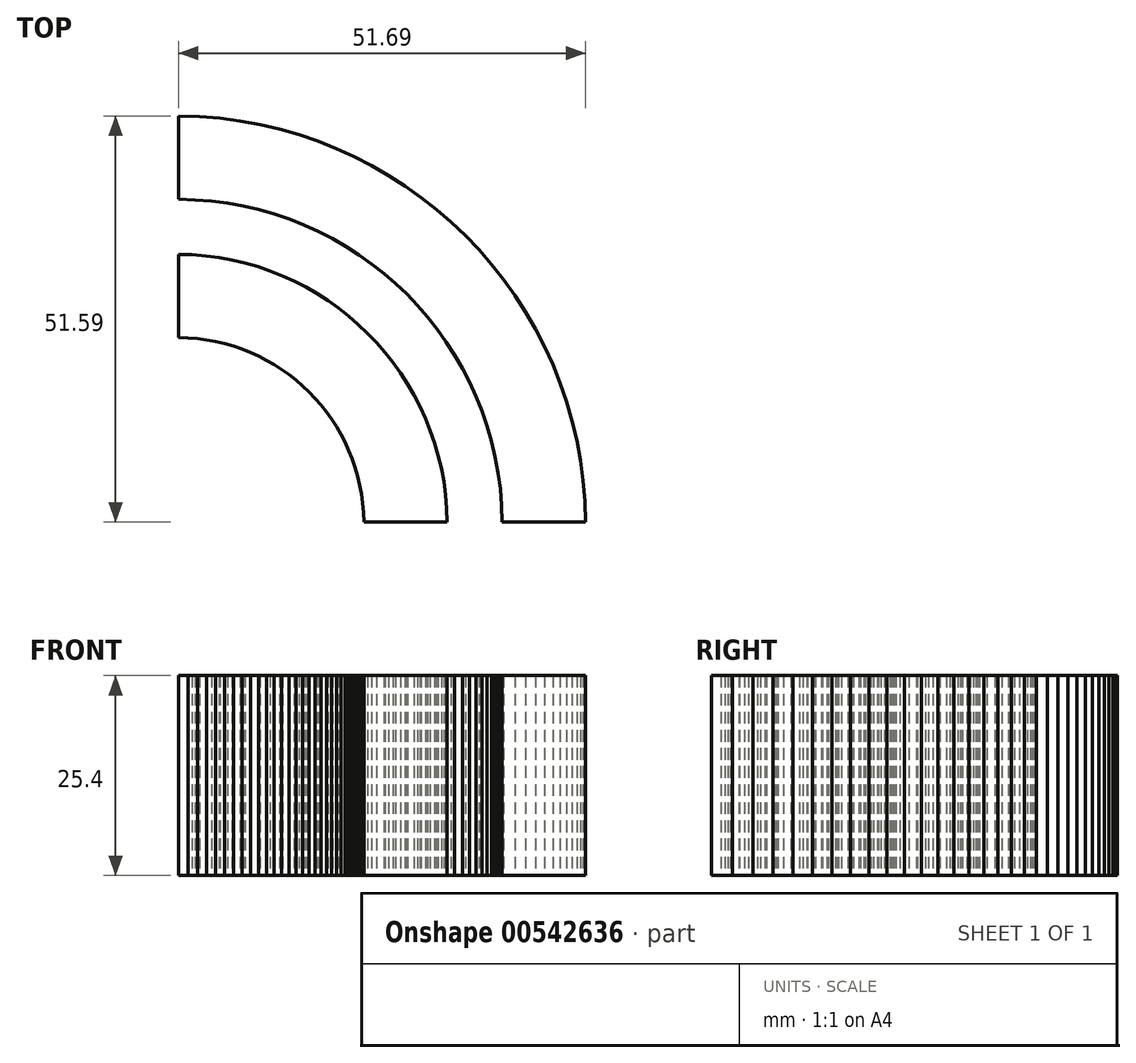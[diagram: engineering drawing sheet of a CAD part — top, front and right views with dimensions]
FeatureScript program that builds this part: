
annotation { "Feature Type Name" : "Feature", "Feature Type Description" : "" }
export const myFeature = defineFeature(function(context is Context, id is Id, definition is map)
    precondition{}
    {
        {
            var Q0;
            Q0=qCreatedBy(makeId("Top.planeOp"),FACE);
            var sketch = newSketch(context, id + "F0", { "sketchPlane" : qUnion([Q0])});
            skLineSegment(sketch, "E0", {"start": v(0.23, 64.99) * mm, "end": v(0.23, 64.66) * mm});
            skLineSegment(sketch, "E1", {"start": v(0.23, 64.66) * mm, "end": v(0.23, 64.33) * mm});
            skLineSegment(sketch, "E2", {"start": v(0.23, 64.33) * mm, "end": v(0.23, 64) * mm});
            skLineSegment(sketch, "E3", {"start": v(0.23, 64) * mm, "end": v(0.23, 63.66) * mm});
            skLineSegment(sketch, "E4", {"start": v(0.23, 63.66) * mm, "end": v(0.23, 63.33) * mm});
            skLineSegment(sketch, "E5", {"start": v(0.23, 63.33) * mm, "end": v(0.23, 63) * mm});
            skLineSegment(sketch, "E6", {"start": v(0.23, 63) * mm, "end": v(0.23, 62.67) * mm});
            skLineSegment(sketch, "E7", {"start": v(0.23, 62.67) * mm, "end": v(0.23, 62.34) * mm});
            skLineSegment(sketch, "E8", {"start": v(0.23, 62.34) * mm, "end": v(0.23, 62.01) * mm});
            skLineSegment(sketch, "E9", {"start": v(0.23, 62.01) * mm, "end": v(0.23, 61.68) * mm});
            skLineSegment(sketch, "E10", {"start": v(0.23, 61.68) * mm, "end": v(0.23, 61.35) * mm});
            skLineSegment(sketch, "E11", {"start": v(0.23, 61.35) * mm, "end": v(0.23, 61.02) * mm});
            skLineSegment(sketch, "E12", {"start": v(0.23, 61.02) * mm, "end": v(0.23, 60.69) * mm});
            skLineSegment(sketch, "E13", {"start": v(0.23, 60.69) * mm, "end": v(0.23, 60.36) * mm});
            skLineSegment(sketch, "E14", {"start": v(0.23, 60.36) * mm, "end": v(0.23, 60.03) * mm});
            skLineSegment(sketch, "E15", {"start": v(0.23, 60.03) * mm, "end": v(0.23, 59.7) * mm});
            skLineSegment(sketch, "E16", {"start": v(0.23, 59.7) * mm, "end": v(0.23, 59.36) * mm});
            skLineSegment(sketch, "E17", {"start": v(0.23, 59.36) * mm, "end": v(0.23, 59.03) * mm});
            skLineSegment(sketch, "E18", {"start": v(0.23, 59.03) * mm, "end": v(0.23, 58.7) * mm});
            skLineSegment(sketch, "E19", {"start": v(0.23, 58.7) * mm, "end": v(0.23, 58.37) * mm});
            skLineSegment(sketch, "E20", {"start": v(0.23, 58.37) * mm, "end": v(0.23, 58.04) * mm});
            skLineSegment(sketch, "E21", {"start": v(0.23, 58.04) * mm, "end": v(0.23, 57.7) * mm});
            skLineSegment(sketch, "E22", {"start": v(0.23, 57.7) * mm, "end": v(0.23, 57.38) * mm});
            skLineSegment(sketch, "E23", {"start": v(0.23, 57.38) * mm, "end": v(0.23, 57.05) * mm});
            skLineSegment(sketch, "E24", {"start": v(0.23, 57.05) * mm, "end": v(0.23, 56.72) * mm});
            skLineSegment(sketch, "E25", {"start": v(0.23, 56.72) * mm, "end": v(0.23, 56.39) * mm});
            skLineSegment(sketch, "E26", {"start": v(0.23, 56.39) * mm, "end": v(0.23, 56.06) * mm});
            skLineSegment(sketch, "E27", {"start": v(0.23, 56.06) * mm, "end": v(0.23, 55.72) * mm});
            skLineSegment(sketch, "E28", {"start": v(0.23, 55.72) * mm, "end": v(0.23, 55.4) * mm});
            skLineSegment(sketch, "E29", {"start": v(0.23, 55.4) * mm, "end": v(0.23, 55.06) * mm});
            skLineSegment(sketch, "E30", {"start": v(0.23, 55.06) * mm, "end": v(0.23, 54.73) * mm});
            skLineSegment(sketch, "E31", {"start": v(0.23, 54.73) * mm, "end": v(0.23, 54.4) * mm});
            skLineSegment(sketch, "E32", {"start": v(0.23, 54.4) * mm, "end": v(1.43, 54.36) * mm});
            skLineSegment(sketch, "E33", {"start": v(1.43, 54.36) * mm, "end": v(2.63, 54.26) * mm});
            skLineSegment(sketch, "E34", {"start": v(2.63, 54.26) * mm, "end": v(3.8, 54.1) * mm});
            skLineSegment(sketch, "E35", {"start": v(3.8, 54.1) * mm, "end": v(4.95, 53.9) * mm});
            skLineSegment(sketch, "E36", {"start": v(4.95, 53.9) * mm, "end": v(6.09, 53.62) * mm});
            skLineSegment(sketch, "E37", {"start": v(6.09, 53.62) * mm, "end": v(7.2, 53.3) * mm});
            skLineSegment(sketch, "E38", {"start": v(7.2, 53.3) * mm, "end": v(8.29, 52.93) * mm});
            skLineSegment(sketch, "E39", {"start": v(8.29, 52.93) * mm, "end": v(9.35, 52.51) * mm});
            skLineSegment(sketch, "E40", {"start": v(9.35, 52.51) * mm, "end": v(10.39, 52.04) * mm});
            skLineSegment(sketch, "E41", {"start": v(10.39, 52.04) * mm, "end": v(11.4, 51.52) * mm});
            skLineSegment(sketch, "E42", {"start": v(11.4, 51.52) * mm, "end": v(12.38, 50.96) * mm});
            skLineSegment(sketch, "E43", {"start": v(12.38, 50.96) * mm, "end": v(13.33, 50.35) * mm});
            skLineSegment(sketch, "E44", {"start": v(13.33, 50.35) * mm, "end": v(14.24, 49.7) * mm});
            skLineSegment(sketch, "E45", {"start": v(14.24, 49.7) * mm, "end": v(15.13, 49) * mm});
            skLineSegment(sketch, "E46", {"start": v(15.13, 49) * mm, "end": v(15.98, 48.27) * mm});
            skLineSegment(sketch, "E47", {"start": v(15.98, 48.27) * mm, "end": v(16.8, 47.5) * mm});
            skLineSegment(sketch, "E48", {"start": v(16.8, 47.5) * mm, "end": v(17.57, 46.7) * mm});
            skLineSegment(sketch, "E49", {"start": v(17.57, 46.7) * mm, "end": v(18.3, 45.84) * mm});
            skLineSegment(sketch, "E50", {"start": v(18.3, 45.84) * mm, "end": v(19, 44.96) * mm});
            skLineSegment(sketch, "E51", {"start": v(19, 44.96) * mm, "end": v(19.66, 44.05) * mm});
            skLineSegment(sketch, "E52", {"start": v(19.66, 44.05) * mm, "end": v(20.27, 43.1) * mm});
            skLineSegment(sketch, "E53", {"start": v(20.27, 43.1) * mm, "end": v(20.84, 42.12) * mm});
            skLineSegment(sketch, "E54", {"start": v(20.84, 42.12) * mm, "end": v(21.36, 41.12) * mm});
            skLineSegment(sketch, "E55", {"start": v(21.36, 41.12) * mm, "end": v(21.84, 40.08) * mm});
            skLineSegment(sketch, "E56", {"start": v(21.84, 40.08) * mm, "end": v(22.26, 39.02) * mm});
            skLineSegment(sketch, "E57", {"start": v(22.26, 39.02) * mm, "end": v(22.64, 37.94) * mm});
            skLineSegment(sketch, "E58", {"start": v(22.64, 37.94) * mm, "end": v(22.96, 36.83) * mm});
            skLineSegment(sketch, "E59", {"start": v(22.96, 36.83) * mm, "end": v(23.23, 35.7) * mm});
            skLineSegment(sketch, "E60", {"start": v(23.23, 35.7) * mm, "end": v(23.45, 34.54) * mm});
            skLineSegment(sketch, "E61", {"start": v(23.45, 34.54) * mm, "end": v(23.61, 33.37) * mm});
            skLineSegment(sketch, "E62", {"start": v(23.61, 33.37) * mm, "end": v(23.72, 32.18) * mm});
            skLineSegment(sketch, "E63", {"start": v(23.72, 32.18) * mm, "end": v(23.77, 30.97) * mm});
            skLineSegment(sketch, "E64", {"start": v(23.77, 30.97) * mm, "end": v(24.1, 30.97) * mm});
            skLineSegment(sketch, "E65", {"start": v(24.1, 30.97) * mm, "end": v(24.43, 30.97) * mm});
            skLineSegment(sketch, "E66", {"start": v(24.43, 30.97) * mm, "end": v(24.76, 30.97) * mm});
            skLineSegment(sketch, "E67", {"start": v(24.76, 30.97) * mm, "end": v(25.09, 30.97) * mm});
            skLineSegment(sketch, "E68", {"start": v(25.09, 30.97) * mm, "end": v(25.42, 30.97) * mm});
            skLineSegment(sketch, "E69", {"start": v(25.42, 30.97) * mm, "end": v(25.75, 30.97) * mm});
            skLineSegment(sketch, "E70", {"start": v(25.75, 30.97) * mm, "end": v(26.08, 30.97) * mm});
            skLineSegment(sketch, "E71", {"start": v(26.08, 30.97) * mm, "end": v(26.41, 30.97) * mm});
            skLineSegment(sketch, "E72", {"start": v(26.41, 30.97) * mm, "end": v(26.74, 30.97) * mm});
            skLineSegment(sketch, "E73", {"start": v(26.74, 30.97) * mm, "end": v(27.07, 30.97) * mm});
            skLineSegment(sketch, "E74", {"start": v(27.07, 30.97) * mm, "end": v(27.4, 30.97) * mm});
            skLineSegment(sketch, "E75", {"start": v(27.4, 30.97) * mm, "end": v(27.74, 30.97) * mm});
            skLineSegment(sketch, "E76", {"start": v(27.74, 30.97) * mm, "end": v(28.07, 30.97) * mm});
            skLineSegment(sketch, "E77", {"start": v(28.07, 30.97) * mm, "end": v(28.4, 30.97) * mm});
            skLineSegment(sketch, "E78", {"start": v(28.4, 30.97) * mm, "end": v(28.73, 30.97) * mm});
            skLineSegment(sketch, "E79", {"start": v(28.73, 30.97) * mm, "end": v(29.06, 30.97) * mm});
            skLineSegment(sketch, "E80", {"start": v(29.06, 30.97) * mm, "end": v(29.4, 30.97) * mm});
            skLineSegment(sketch, "E81", {"start": v(29.4, 30.97) * mm, "end": v(29.72, 30.97) * mm});
            skLineSegment(sketch, "E82", {"start": v(29.72, 30.97) * mm, "end": v(30.05, 30.97) * mm});
            skLineSegment(sketch, "E83", {"start": v(30.05, 30.97) * mm, "end": v(30.38, 30.97) * mm});
            skLineSegment(sketch, "E84", {"start": v(30.38, 30.97) * mm, "end": v(30.71, 30.97) * mm});
            skLineSegment(sketch, "E85", {"start": v(30.71, 30.97) * mm, "end": v(31.05, 30.97) * mm});
            skLineSegment(sketch, "E86", {"start": v(31.05, 30.97) * mm, "end": v(31.38, 30.97) * mm});
            skLineSegment(sketch, "E87", {"start": v(31.38, 30.97) * mm, "end": v(31.7, 30.97) * mm});
            skLineSegment(sketch, "E88", {"start": v(31.7, 30.97) * mm, "end": v(32.04, 30.97) * mm});
            skLineSegment(sketch, "E89", {"start": v(32.04, 30.97) * mm, "end": v(32.37, 30.97) * mm});
            skLineSegment(sketch, "E90", {"start": v(32.37, 30.97) * mm, "end": v(32.7, 30.97) * mm});
            skLineSegment(sketch, "E91", {"start": v(32.7, 30.97) * mm, "end": v(33.03, 30.97) * mm});
            skLineSegment(sketch, "E92", {"start": v(33.03, 30.97) * mm, "end": v(33.36, 30.97) * mm});
            skLineSegment(sketch, "E93", {"start": v(33.36, 30.97) * mm, "end": v(33.7, 30.97) * mm});
            skLineSegment(sketch, "E94", {"start": v(33.7, 30.97) * mm, "end": v(34.02, 30.97) * mm});
            skLineSegment(sketch, "E95", {"start": v(34.02, 30.97) * mm, "end": v(34.35, 30.97) * mm});
            skLineSegment(sketch, "E96", {"start": v(34.35, 30.97) * mm, "end": v(34.3, 32.71) * mm});
            skLineSegment(sketch, "E97", {"start": v(34.3, 32.71) * mm, "end": v(34.15, 34.43) * mm});
            skLineSegment(sketch, "E98", {"start": v(34.15, 34.43) * mm, "end": v(33.91, 36.13) * mm});
            skLineSegment(sketch, "E99", {"start": v(33.91, 36.13) * mm, "end": v(33.6, 37.8) * mm});
            skLineSegment(sketch, "E100", {"start": v(33.6, 37.8) * mm, "end": v(33.2, 39.43) * mm});
            skLineSegment(sketch, "E101", {"start": v(33.2, 39.43) * mm, "end": v(32.74, 41.04) * mm});
            skLineSegment(sketch, "E102", {"start": v(32.74, 41.04) * mm, "end": v(32.2, 42.61) * mm});
            skLineSegment(sketch, "E103", {"start": v(32.2, 42.61) * mm, "end": v(31.57, 44.15) * mm});
            skLineSegment(sketch, "E104", {"start": v(31.57, 44.15) * mm, "end": v(30.88, 45.65) * mm});
            skLineSegment(sketch, "E105", {"start": v(30.88, 45.65) * mm, "end": v(30.12, 47.12) * mm});
            skLineSegment(sketch, "E106", {"start": v(30.12, 47.12) * mm, "end": v(29.3, 48.54) * mm});
            skLineSegment(sketch, "E107", {"start": v(29.3, 48.54) * mm, "end": v(28.4, 49.91) * mm});
            skLineSegment(sketch, "E108", {"start": v(28.4, 49.91) * mm, "end": v(27.45, 51.24) * mm});
            skLineSegment(sketch, "E109", {"start": v(27.45, 51.24) * mm, "end": v(26.43, 52.53) * mm});
            skLineSegment(sketch, "E110", {"start": v(26.43, 52.53) * mm, "end": v(25.36, 53.76) * mm});
            skLineSegment(sketch, "E111", {"start": v(25.36, 53.76) * mm, "end": v(24.23, 54.94) * mm});
            skLineSegment(sketch, "E112", {"start": v(24.23, 54.94) * mm, "end": v(23.05, 56.07) * mm});
            skLineSegment(sketch, "E113", {"start": v(23.05, 56.07) * mm, "end": v(21.81, 57.14) * mm});
            skLineSegment(sketch, "E114", {"start": v(21.81, 57.14) * mm, "end": v(20.53, 58.15) * mm});
            skLineSegment(sketch, "E115", {"start": v(20.53, 58.15) * mm, "end": v(19.2, 59.1) * mm});
            skLineSegment(sketch, "E116", {"start": v(19.2, 59.1) * mm, "end": v(17.81, 59.98) * mm});
            skLineSegment(sketch, "E117", {"start": v(17.81, 59.98) * mm, "end": v(16.39, 60.8) * mm});
            skLineSegment(sketch, "E118", {"start": v(16.39, 60.8) * mm, "end": v(14.92, 61.56) * mm});
            skLineSegment(sketch, "E119", {"start": v(14.92, 61.56) * mm, "end": v(13.42, 62.25) * mm});
            skLineSegment(sketch, "E120", {"start": v(13.42, 62.25) * mm, "end": v(11.88, 62.86) * mm});
            skLineSegment(sketch, "E121", {"start": v(11.88, 62.86) * mm, "end": v(10.3, 63.4) * mm});
            skLineSegment(sketch, "E122", {"start": v(10.3, 63.4) * mm, "end": v(8.7, 63.87) * mm});
            skLineSegment(sketch, "E123", {"start": v(8.7, 63.87) * mm, "end": v(7.05, 64.26) * mm});
            skLineSegment(sketch, "E124", {"start": v(7.05, 64.26) * mm, "end": v(5.38, 64.56) * mm});
            skLineSegment(sketch, "E125", {"start": v(5.38, 64.56) * mm, "end": v(3.69, 64.8) * mm});
            skLineSegment(sketch, "E126", {"start": v(3.69, 64.8) * mm, "end": v(1.97, 64.93) * mm});
            skLineSegment(sketch, "E127", {"start": v(1.97, 64.93) * mm, "end": v(0.23, 64.99) * mm});
            skLineSegment(sketch, "E128", {"start": v(0.23, 82.56) * mm, "end": v(0.23, 82.23) * mm});
            skLineSegment(sketch, "E129", {"start": v(0.23, 82.23) * mm, "end": v(0.23, 81.9) * mm});
            skLineSegment(sketch, "E130", {"start": v(0.23, 81.9) * mm, "end": v(0.23, 81.56) * mm});
            skLineSegment(sketch, "E131", {"start": v(0.23, 81.56) * mm, "end": v(0.23, 81.23) * mm});
            skLineSegment(sketch, "E132", {"start": v(0.23, 81.23) * mm, "end": v(0.23, 80.9) * mm});
            skLineSegment(sketch, "E133", {"start": v(0.23, 80.9) * mm, "end": v(0.23, 80.57) * mm});
            skLineSegment(sketch, "E134", {"start": v(0.23, 80.57) * mm, "end": v(0.23, 80.24) * mm});
            skLineSegment(sketch, "E135", {"start": v(0.23, 80.24) * mm, "end": v(0.23, 79.91) * mm});
            skLineSegment(sketch, "E136", {"start": v(0.23, 79.91) * mm, "end": v(0.23, 79.58) * mm});
            skLineSegment(sketch, "E137", {"start": v(0.23, 79.58) * mm, "end": v(0.23, 79.25) * mm});
            skLineSegment(sketch, "E138", {"start": v(0.23, 79.25) * mm, "end": v(0.23, 78.92) * mm});
            skLineSegment(sketch, "E139", {"start": v(0.23, 78.92) * mm, "end": v(0.23, 78.59) * mm});
            skLineSegment(sketch, "E140", {"start": v(0.23, 78.59) * mm, "end": v(0.23, 78.26) * mm});
            skLineSegment(sketch, "E141", {"start": v(0.23, 78.26) * mm, "end": v(0.23, 77.93) * mm});
            skLineSegment(sketch, "E142", {"start": v(0.23, 77.93) * mm, "end": v(0.23, 77.6) * mm});
            skLineSegment(sketch, "E143", {"start": v(0.23, 77.6) * mm, "end": v(0.23, 77.26) * mm});
            skLineSegment(sketch, "E144", {"start": v(0.23, 77.26) * mm, "end": v(0.23, 76.93) * mm});
            skLineSegment(sketch, "E145", {"start": v(0.23, 76.93) * mm, "end": v(0.23, 76.6) * mm});
            skLineSegment(sketch, "E146", {"start": v(0.23, 76.6) * mm, "end": v(0.23, 76.27) * mm});
            skLineSegment(sketch, "E147", {"start": v(0.23, 76.27) * mm, "end": v(0.23, 75.94) * mm});
            skLineSegment(sketch, "E148", {"start": v(0.23, 75.94) * mm, "end": v(0.23, 75.61) * mm});
            skLineSegment(sketch, "E149", {"start": v(0.23, 75.61) * mm, "end": v(0.23, 75.28) * mm});
            skLineSegment(sketch, "E150", {"start": v(0.23, 75.28) * mm, "end": v(0.23, 74.95) * mm});
            skLineSegment(sketch, "E151", {"start": v(0.23, 74.95) * mm, "end": v(0.23, 74.62) * mm});
            skLineSegment(sketch, "E152", {"start": v(0.23, 74.62) * mm, "end": v(0.23, 74.29) * mm});
            skLineSegment(sketch, "E153", {"start": v(0.23, 74.29) * mm, "end": v(0.23, 73.96) * mm});
            skLineSegment(sketch, "E154", {"start": v(0.23, 73.96) * mm, "end": v(0.23, 73.63) * mm});
            skLineSegment(sketch, "E155", {"start": v(0.23, 73.63) * mm, "end": v(0.23, 73.3) * mm});
            skLineSegment(sketch, "E156", {"start": v(0.23, 73.3) * mm, "end": v(0.23, 72.96) * mm});
            skLineSegment(sketch, "E157", {"start": v(0.23, 72.96) * mm, "end": v(0.23, 72.63) * mm});
            skLineSegment(sketch, "E158", {"start": v(0.23, 72.63) * mm, "end": v(0.23, 72.3) * mm});
            skLineSegment(sketch, "E159", {"start": v(0.23, 72.3) * mm, "end": v(0.23, 71.97) * mm});
            skLineSegment(sketch, "E160", {"start": v(0.23, 71.97) * mm, "end": v(2.34, 71.9) * mm});
            skLineSegment(sketch, "E161", {"start": v(2.34, 71.9) * mm, "end": v(4.42, 71.74) * mm});
            skLineSegment(sketch, "E162", {"start": v(4.42, 71.74) * mm, "end": v(6.48, 71.47) * mm});
            skLineSegment(sketch, "E163", {"start": v(6.48, 71.47) * mm, "end": v(8.5, 71.1) * mm});
            skLineSegment(sketch, "E164", {"start": v(8.5, 71.1) * mm, "end": v(10.48, 70.64) * mm});
            skLineSegment(sketch, "E165", {"start": v(10.48, 70.64) * mm, "end": v(12.43, 70.09) * mm});
            skLineSegment(sketch, "E166", {"start": v(12.43, 70.09) * mm, "end": v(14.33, 69.44) * mm});
            skLineSegment(sketch, "E167", {"start": v(14.33, 69.44) * mm, "end": v(16.2, 68.7) * mm});
            skLineSegment(sketch, "E168", {"start": v(16.2, 68.7) * mm, "end": v(18, 67.88) * mm});
            skLineSegment(sketch, "E169", {"start": v(18, 67.88) * mm, "end": v(19.77, 66.97) * mm});
            skLineSegment(sketch, "E170", {"start": v(19.77, 66.97) * mm, "end": v(21.49, 65.99) * mm});
            skLineSegment(sketch, "E171", {"start": v(21.49, 65.99) * mm, "end": v(23.15, 64.92) * mm});
            skLineSegment(sketch, "E172", {"start": v(23.15, 64.92) * mm, "end": v(24.76, 63.78) * mm});
            skLineSegment(sketch, "E173", {"start": v(24.76, 63.78) * mm, "end": v(26.3, 62.57) * mm});
            skLineSegment(sketch, "E174", {"start": v(26.3, 62.57) * mm, "end": v(27.8, 61.28) * mm});
            skLineSegment(sketch, "E175", {"start": v(27.8, 61.28) * mm, "end": v(29.22, 59.93) * mm});
            skLineSegment(sketch, "E176", {"start": v(29.22, 59.93) * mm, "end": v(30.58, 58.5) * mm});
            skLineSegment(sketch, "E177", {"start": v(30.58, 58.5) * mm, "end": v(31.87, 57.02) * mm});
            skLineSegment(sketch, "E178", {"start": v(31.87, 57.02) * mm, "end": v(33.08, 55.48) * mm});
            skLineSegment(sketch, "E179", {"start": v(33.08, 55.48) * mm, "end": v(34.23, 53.87) * mm});
            skLineSegment(sketch, "E180", {"start": v(34.23, 53.87) * mm, "end": v(35.3, 52.21) * mm});
            skLineSegment(sketch, "E181", {"start": v(35.3, 52.21) * mm, "end": v(36.3, 50.5) * mm});
            skLineSegment(sketch, "E182", {"start": v(36.3, 50.5) * mm, "end": v(37.2, 48.74) * mm});
            skLineSegment(sketch, "E183", {"start": v(37.2, 48.74) * mm, "end": v(38.03, 46.92) * mm});
            skLineSegment(sketch, "E184", {"start": v(38.03, 46.92) * mm, "end": v(38.77, 45.06) * mm});
            skLineSegment(sketch, "E185", {"start": v(38.77, 45.06) * mm, "end": v(39.42, 43.16) * mm});
            skLineSegment(sketch, "E186", {"start": v(39.42, 43.16) * mm, "end": v(39.98, 41.22) * mm});
            skLineSegment(sketch, "E187", {"start": v(39.98, 41.22) * mm, "end": v(40.45, 39.24) * mm});
            skLineSegment(sketch, "E188", {"start": v(40.45, 39.24) * mm, "end": v(40.82, 37.22) * mm});
            skLineSegment(sketch, "E189", {"start": v(40.82, 37.22) * mm, "end": v(41.1, 35.17) * mm});
            skLineSegment(sketch, "E190", {"start": v(41.1, 35.17) * mm, "end": v(41.27, 33.08) * mm});
            skLineSegment(sketch, "E191", {"start": v(41.27, 33.08) * mm, "end": v(41.34, 30.97) * mm});
            skLineSegment(sketch, "E192", {"start": v(41.34, 30.97) * mm, "end": v(41.67, 30.97) * mm});
            skLineSegment(sketch, "E193", {"start": v(41.67, 30.97) * mm, "end": v(42, 30.97) * mm});
            skLineSegment(sketch, "E194", {"start": v(42, 30.97) * mm, "end": v(42.33, 30.97) * mm});
            skLineSegment(sketch, "E195", {"start": v(42.33, 30.97) * mm, "end": v(42.66, 30.97) * mm});
            skLineSegment(sketch, "E196", {"start": v(42.66, 30.97) * mm, "end": v(43, 30.97) * mm});
            skLineSegment(sketch, "E197", {"start": v(43, 30.97) * mm, "end": v(43.32, 30.97) * mm});
            skLineSegment(sketch, "E198", {"start": v(43.32, 30.97) * mm, "end": v(43.65, 30.97) * mm});
            skLineSegment(sketch, "E199", {"start": v(43.65, 30.97) * mm, "end": v(43.99, 30.97) * mm});
            skLineSegment(sketch, "E200", {"start": v(43.99, 30.97) * mm, "end": v(44.32, 30.97) * mm});
            skLineSegment(sketch, "E201", {"start": v(44.32, 30.97) * mm, "end": v(44.65, 30.97) * mm});
            skLineSegment(sketch, "E202", {"start": v(44.65, 30.97) * mm, "end": v(44.98, 30.97) * mm});
            skLineSegment(sketch, "E203", {"start": v(44.98, 30.97) * mm, "end": v(45.3, 30.97) * mm});
            skLineSegment(sketch, "E204", {"start": v(45.3, 30.97) * mm, "end": v(45.64, 30.97) * mm});
            skLineSegment(sketch, "E205", {"start": v(45.64, 30.97) * mm, "end": v(45.97, 30.97) * mm});
            skLineSegment(sketch, "E206", {"start": v(45.97, 30.97) * mm, "end": v(46.3, 30.97) * mm});
            skLineSegment(sketch, "E207", {"start": v(46.3, 30.97) * mm, "end": v(46.63, 30.97) * mm});
            skLineSegment(sketch, "E208", {"start": v(46.63, 30.97) * mm, "end": v(46.96, 30.97) * mm});
            skLineSegment(sketch, "E209", {"start": v(46.96, 30.97) * mm, "end": v(47.3, 30.97) * mm});
            skLineSegment(sketch, "E210", {"start": v(47.3, 30.97) * mm, "end": v(47.62, 30.97) * mm});
            skLineSegment(sketch, "E211", {"start": v(47.62, 30.97) * mm, "end": v(47.95, 30.97) * mm});
            skLineSegment(sketch, "E212", {"start": v(47.95, 30.97) * mm, "end": v(48.28, 30.97) * mm});
            skLineSegment(sketch, "E213", {"start": v(48.28, 30.97) * mm, "end": v(48.62, 30.97) * mm});
            skLineSegment(sketch, "E214", {"start": v(48.62, 30.97) * mm, "end": v(48.95, 30.97) * mm});
            skLineSegment(sketch, "E215", {"start": v(48.95, 30.97) * mm, "end": v(49.28, 30.97) * mm});
            skLineSegment(sketch, "E216", {"start": v(49.28, 30.97) * mm, "end": v(49.6, 30.97) * mm});
            skLineSegment(sketch, "E217", {"start": v(49.6, 30.97) * mm, "end": v(49.94, 30.97) * mm});
            skLineSegment(sketch, "E218", {"start": v(49.94, 30.97) * mm, "end": v(50.27, 30.97) * mm});
            skLineSegment(sketch, "E219", {"start": v(50.27, 30.97) * mm, "end": v(50.6, 30.97) * mm});
            skLineSegment(sketch, "E220", {"start": v(50.6, 30.97) * mm, "end": v(50.93, 30.97) * mm});
            skLineSegment(sketch, "E221", {"start": v(50.93, 30.97) * mm, "end": v(51.26, 30.97) * mm});
            skLineSegment(sketch, "E222", {"start": v(51.26, 30.97) * mm, "end": v(51.6, 30.97) * mm});
            skLineSegment(sketch, "E223", {"start": v(51.6, 30.97) * mm, "end": v(51.92, 30.97) * mm});
            skLineSegment(sketch, "E224", {"start": v(51.92, 30.97) * mm, "end": v(51.84, 33.62) * mm});
            skLineSegment(sketch, "E225", {"start": v(51.84, 33.62) * mm, "end": v(51.62, 36.23) * mm});
            skLineSegment(sketch, "E226", {"start": v(51.62, 36.23) * mm, "end": v(51.28, 38.8) * mm});
            skLineSegment(sketch, "E227", {"start": v(51.28, 38.8) * mm, "end": v(50.81, 41.33) * mm});
            skLineSegment(sketch, "E228", {"start": v(50.81, 41.33) * mm, "end": v(50.22, 43.82) * mm});
            skLineSegment(sketch, "E229", {"start": v(50.22, 43.82) * mm, "end": v(49.52, 46.26) * mm});
            skLineSegment(sketch, "E230", {"start": v(49.52, 46.26) * mm, "end": v(48.7, 48.65) * mm});
            skLineSegment(sketch, "E231", {"start": v(48.7, 48.65) * mm, "end": v(47.76, 50.99) * mm});
            skLineSegment(sketch, "E232", {"start": v(47.76, 50.99) * mm, "end": v(46.72, 53.27) * mm});
            skLineSegment(sketch, "E233", {"start": v(46.72, 53.27) * mm, "end": v(45.57, 55.49) * mm});
            skLineSegment(sketch, "E234", {"start": v(45.57, 55.49) * mm, "end": v(44.32, 57.65) * mm});
            skLineSegment(sketch, "E235", {"start": v(44.32, 57.65) * mm, "end": v(42.97, 59.73) * mm});
            skLineSegment(sketch, "E236", {"start": v(42.97, 59.73) * mm, "end": v(41.53, 61.75) * mm});
            skLineSegment(sketch, "E237", {"start": v(41.53, 61.75) * mm, "end": v(40, 63.7) * mm});
            skLineSegment(sketch, "E238", {"start": v(40, 63.7) * mm, "end": v(38.37, 65.57) * mm});
            skLineSegment(sketch, "E239", {"start": v(38.37, 65.57) * mm, "end": v(36.65, 67.36) * mm});
            skLineSegment(sketch, "E240", {"start": v(36.65, 67.36) * mm, "end": v(34.86, 69.07) * mm});
            skLineSegment(sketch, "E241", {"start": v(34.86, 69.07) * mm, "end": v(32.99, 70.7) * mm});
            skLineSegment(sketch, "E242", {"start": v(32.99, 70.7) * mm, "end": v(31.04, 72.22) * mm});
            skLineSegment(sketch, "E243", {"start": v(31.04, 72.22) * mm, "end": v(29.01, 73.66) * mm});
            skLineSegment(sketch, "E244", {"start": v(29.01, 73.66) * mm, "end": v(26.92, 75) * mm});
            skLineSegment(sketch, "E245", {"start": v(26.92, 75) * mm, "end": v(24.76, 76.25) * mm});
            skLineSegment(sketch, "E246", {"start": v(24.76, 76.25) * mm, "end": v(22.54, 77.4) * mm});
            skLineSegment(sketch, "E247", {"start": v(22.54, 77.4) * mm, "end": v(20.26, 78.44) * mm});
            skLineSegment(sketch, "E248", {"start": v(20.26, 78.44) * mm, "end": v(17.92, 79.36) * mm});
            skLineSegment(sketch, "E249", {"start": v(17.92, 79.36) * mm, "end": v(15.53, 80.18) * mm});
            skLineSegment(sketch, "E250", {"start": v(15.53, 80.18) * mm, "end": v(13.08, 80.88) * mm});
            skLineSegment(sketch, "E251", {"start": v(13.08, 80.88) * mm, "end": v(10.6, 81.47) * mm});
            skLineSegment(sketch, "E252", {"start": v(10.6, 81.47) * mm, "end": v(8.06, 81.93) * mm});
            skLineSegment(sketch, "E253", {"start": v(8.06, 81.93) * mm, "end": v(5.48, 82.27) * mm});
            skLineSegment(sketch, "E254", {"start": v(5.48, 82.27) * mm, "end": v(2.87, 82.48) * mm});
            skLineSegment(sketch, "E255", {"start": v(2.87, 82.48) * mm, "end": v(0.23, 82.56) * mm});
            skSolve(sketch);
        }
        {
            var Q0;
            Q0 = qSketchRegion(id + "F0", true);
            extrude(context, id + "F1", {"entities" : qUnion([Q0]), "depth" : 25.4 * mm, "offsetDistance" : 25.4 * mm});
        }
    });
